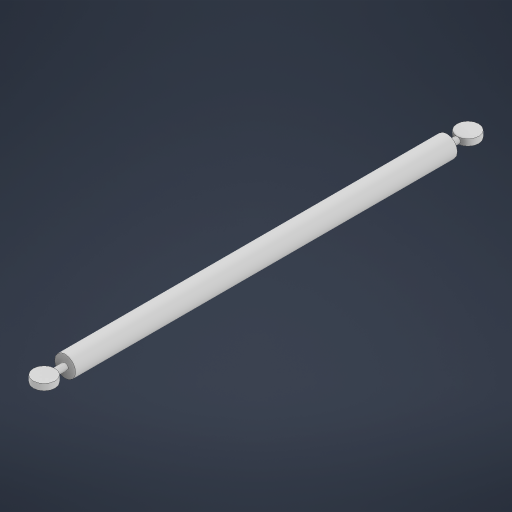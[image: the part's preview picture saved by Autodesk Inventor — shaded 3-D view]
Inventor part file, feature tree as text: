
AUTODESK INVENTOR PART (.ipt)
format: ipt  version: 2023 (Build 270158000, 158)  size: 256,512 bytes
history: native  units: in
note: dims shown in document units (in); Inventor stores cm internally (conversion verified against a paired STEP export)
features: extrude x3, sketch x3, plane x1, mirror x1
ambient origin geometry x8: Origin, YZ Plane, XZ Plane, XY Plane, X Axis, Y Axis, Z Axis, Center Point
bodies: Solid1 (feature_tree)
feature tree (8):
  extrude  "Extrusion1"  Depth=45.5in TaperAngle=0.0deg
  extrude  "Extrusion2"  Depth=0.75in TaperAngle=0.0deg
  extrude  "Extrusion3"  Depth=0.75in
  plane  "Work Plane1"
  mirror  "Mirror1"
  sketch  "Sketch1"  dims[d0=2.5in d1=45.5in d2=0.0in]
  sketch  "Sketch2"  dims[d3=0.75in d4=2.0in d5=0.0in]
  sketch  "Sketch3"  dims[d6=2.5in d7=2.6in d8=0.75in d9=0.0in]
